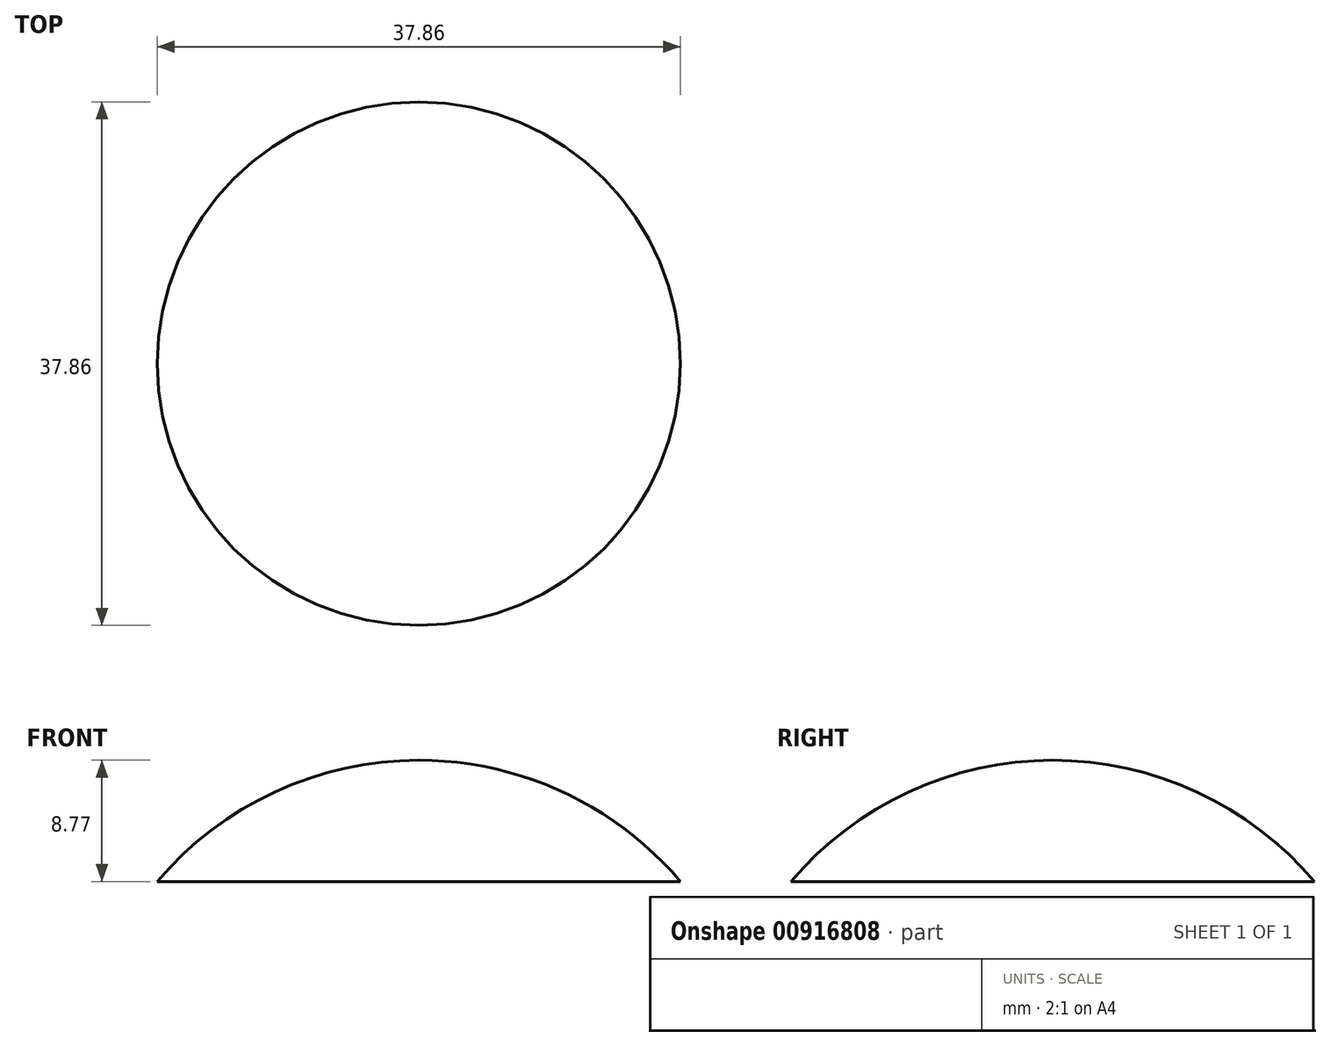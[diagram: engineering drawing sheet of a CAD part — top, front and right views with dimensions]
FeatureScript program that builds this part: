
annotation { "Feature Type Name" : "Feature", "Feature Type Description" : "" }
export const myFeature = defineFeature(function(context is Context, id is Id, definition is map)
    precondition{}
    {
        {
            var Q0;
            Q0=qCreatedBy(makeId("Front.planeOp"),FACE);
            var sketch = newSketch(context, id + "F0", { "sketchPlane" : qUnion([Q0])});
            skArc(sketch, "E0", {"start": v(18.93, 0) * mm, "mid": v(10.43, 6.47) * mm, "end": v(0, 8.77) * mm});
            skLineSegment(sketch, "E1", {"start": v(0, 0) * mm, "end": v(18.93, 0) * mm});
            skLineSegment(sketch, "E2", {"start": v(0, 8.77) * mm, "end": v(0, 0) * mm});
            skPoint(sketch, "E3.orphan", {"position": v(-18.93, 0) * mm});
            skSolve(sketch);
        }
        {
            var Q0;
            Q0=makeQuery(id+"F0.imprint","IMPRINT",FACE,{"disambiguationData":[TD([[makeQuery(id+"F0.imprint","IMPRINT",EDGE,{"derivedFrom":sQuery(id+"F0.wireOp",EDGE,"E0")}),1.0]])]});
            var Q1;
            Q1=sQuery(id+"F0.wireOp",EDGE,"E2");
            revolve(context, id + "F1", {"surfaceOperationType" : NewSurfaceOperationType.NEW, "entities" : qUnion([Q0]), "axis" : qUnion([Q1]), "revolveType" : RevolveType.FULL});
        }
    });
